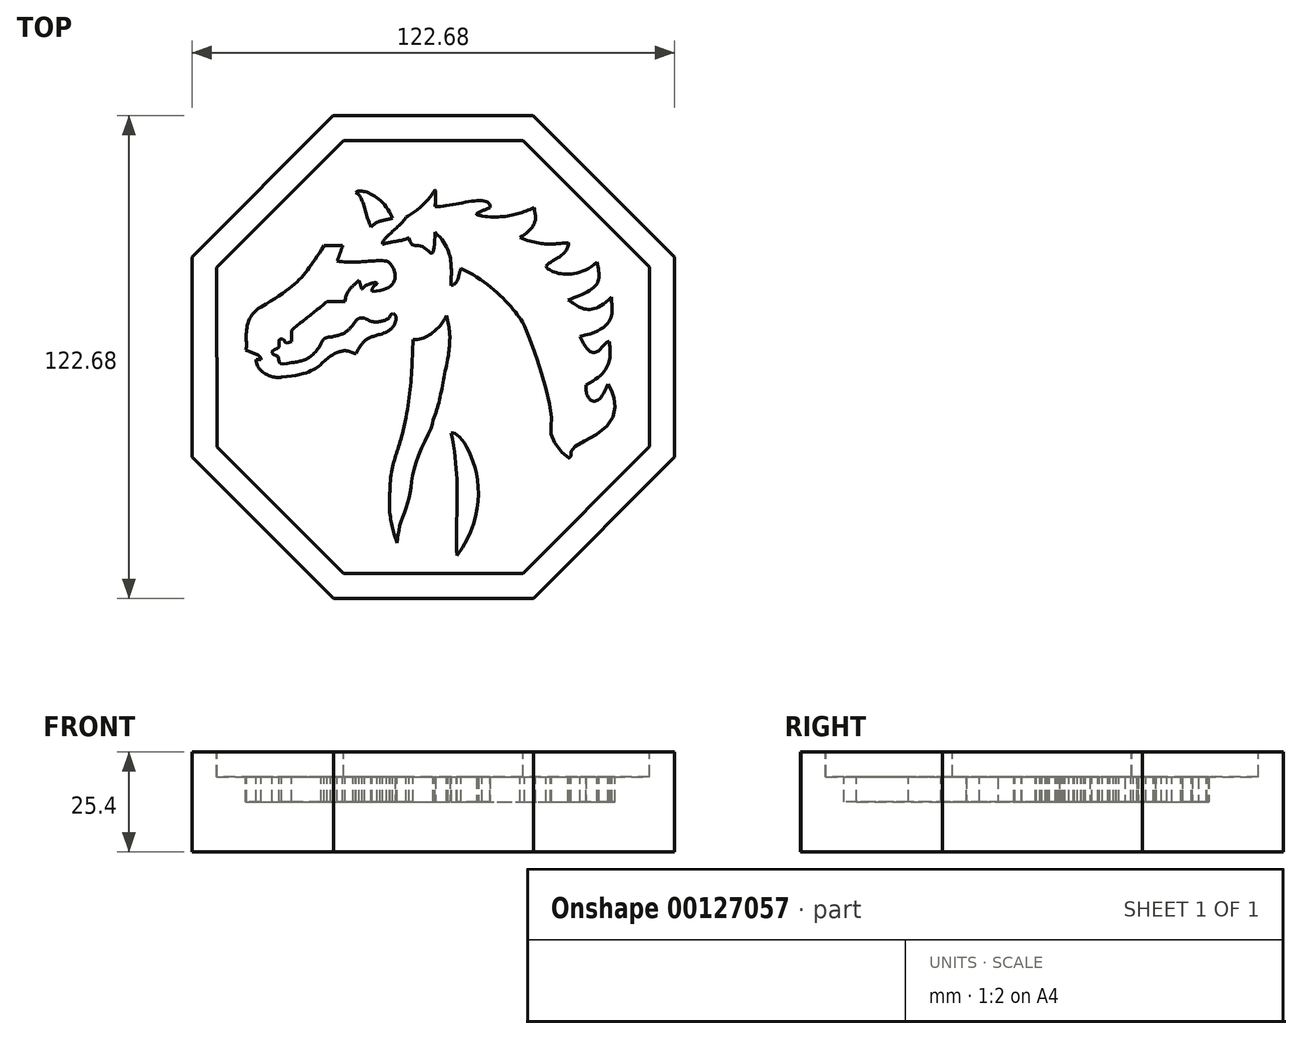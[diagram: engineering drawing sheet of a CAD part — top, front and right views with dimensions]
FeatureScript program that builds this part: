
annotation { "Feature Type Name" : "Feature", "Feature Type Description" : "" }
export const myFeature = defineFeature(function(context is Context, id is Id, definition is map)
    precondition{}
    {
        {
            var Q0;
            Q0=qCreatedBy(makeId("Top.planeOp"),FACE);
            var sketch = newSketch(context, id + "F0", { "sketchPlane" : qUnion([Q0])});
            skCircle(sketch, "E0.cCircle", {"center": v(0, 0) * mm, "radius": 61.32 * mm, "construction": true});
            skLineSegment(sketch, "E0.0", {"start": v(-61.3, -25.44) * mm, "end": v(-61.34, 25.36) * mm});
            skLineSegment(sketch, "E0.1", {"start": v(-61.34, 25.36) * mm, "end": v(-25.44, 61.3) * mm});
            skLineSegment(sketch, "E0.2", {"start": v(-25.44, 61.3) * mm, "end": v(25.36, 61.34) * mm});
            skLineSegment(sketch, "E0.3", {"start": v(25.36, 61.34) * mm, "end": v(61.3, 25.44) * mm});
            skLineSegment(sketch, "E0.4", {"start": v(61.3, 25.44) * mm, "end": v(61.34, -25.36) * mm});
            skLineSegment(sketch, "E0.5", {"start": v(61.34, -25.36) * mm, "end": v(25.44, -61.3) * mm});
            skLineSegment(sketch, "E0.6", {"start": v(25.44, -61.3) * mm, "end": v(-25.36, -61.34) * mm});
            skLineSegment(sketch, "E0.7", {"start": v(-25.36, -61.34) * mm, "end": v(-61.3, -25.44) * mm});
            skPoint(sketch, "E0.0.midPoint", {"position": v(-61.32, -0.04) * mm});
            skSolve(sketch);
        }
        {
            var Q0;
            Q0=qSketchRegion(id+"F0",true);
            extrude(context, id + "F1", {"entities" : qUnion([Q0]), "depth" : 25.4 * mm});
        }
        {
            var Q0;
            Q0=makeQuery(id+"F1.opExtrude","CAP_FACE",FACE,{"disambiguationData":[OSD([sQuery(id+"F0.wireOp",EDGE,"E0.0"),sQuery(id+"F0.wireOp",EDGE,"E0.1"),sQuery(id+"F0.wireOp",EDGE,"E0.2"),sQuery(id+"F0.wireOp",EDGE,"E0.3"),sQuery(id+"F0.wireOp",EDGE,"E0.4"),sQuery(id+"F0.wireOp",EDGE,"E0.5"),sQuery(id+"F0.wireOp",EDGE,"E0.6"),sQuery(id+"F0.wireOp",EDGE,"E0.7")])],"isStart":false});
            var sketch = newSketch(context, id + "F2", { "sketchPlane" : qUnion([Q0])});
            skLineSegment(sketch, "E1.0", {"start": v(-54.96, -22.8) * mm, "end": v(-54.99, 22.73) * mm});
            skLineSegment(sketch, "E1.1", {"start": v(-22.73, -54.99) * mm, "end": v(-54.96, -22.8) * mm});
            skLineSegment(sketch, "E1.2", {"start": v(-54.99, 22.73) * mm, "end": v(-22.8, 54.96) * mm});
            skLineSegment(sketch, "E1.3", {"start": v(22.8, -54.96) * mm, "end": v(-22.73, -54.99) * mm});
            skLineSegment(sketch, "E1.4", {"start": v(-22.8, 54.96) * mm, "end": v(22.73, 54.99) * mm});
            skLineSegment(sketch, "E1.5", {"start": v(22.73, 54.99) * mm, "end": v(54.96, 22.8) * mm});
            skLineSegment(sketch, "E1.6", {"start": v(54.96, 22.8) * mm, "end": v(54.99, -22.73) * mm});
            skLineSegment(sketch, "E1.7", {"start": v(54.99, -22.73) * mm, "end": v(22.8, -54.96) * mm});
            skSolve(sketch);
        }
        {
            var Q0;
            Q0=qSketchRegion(id+"F2",true);
            extrude(context, id + "F3", {"entities" : qUnion([Q0]), "operationType" : NewBodyOperationType.REMOVE, "oppositeDirection" : true, "depth" : 6.35 * mm});
        }
        {
            var Q0;
            Q0=makeQuery(id+"F3.boolean.opBoolean","COPY",FACE,{"derivedFrom":makeQuery(id+"F3.opExtrude","CAP_FACE",FACE,{"disambiguationData":[OSD([sQuery(id+"F2.wireOp",EDGE,"E1.0"),sQuery(id+"F2.wireOp",EDGE,"E1.1"),sQuery(id+"F2.wireOp",EDGE,"E1.2"),sQuery(id+"F2.wireOp",EDGE,"E1.3"),sQuery(id+"F2.wireOp",EDGE,"E1.4"),sQuery(id+"F2.wireOp",EDGE,"E1.5"),sQuery(id+"F2.wireOp",EDGE,"E1.6"),sQuery(id+"F2.wireOp",EDGE,"E1.7")])],"isStart":false})});
            var sketch = newSketch(context, id + "F4", { "sketchPlane" : qUnion([Q0])});
            skFitSpline(sketch, "E2", {"points": [v(-5.15, 4.45) * mm, v(3.35, 10.57) * mm], "startDerivative": vector(12.96, -0.8) * mm, "endDerivative": vector(2.4, 5.98) * mm});
            skFitSpline(sketch, "E3", {"points": [v(3.35, 10.57) * mm, v(3.8, 0) * mm], "startDerivative": vector(4.19, -14.96) * mm, "endDerivative": vector(-0.8, -9.17) * mm});
            skFitSpline(sketch, "E4", {"points": [v(-5.15, 4.45) * mm, v(-7.68, -18.75) * mm], "startDerivative": vector(-0.8, -24.13) * mm, "endDerivative": vector(-6.18, -26.52) * mm});
            skFitSpline(sketch, "E5", {"points": [v(-7.68, -18.75) * mm, v(-11.02, -33.98) * mm], "startDerivative": vector(-4.18, -17.48) * mm, "endDerivative": vector(-0.53, -21.3) * mm});
            skFitSpline(sketch, "E6", {"points": [v(-11.02, -33.98) * mm, v(-9.16, -47.18) * mm], "startDerivative": vector(-1.6, -17.3) * mm, "endDerivative": vector(4, -9.85) * mm});
            skFitSpline(sketch, "E7", {"points": [v(-9.16, -47.18) * mm, v(-8.36, -42.41) * mm, v(-6.24, -36.2) * mm, v(-4.38, -26.74) * mm, v(0, -15.97) * mm], "startDerivative": vector(2.5, 24.1) * mm, "endDerivative": vector(0, 17.06) * mm});
            skFitSpline(sketch, "E8", {"points": [v(0, -15.97) * mm, v(3.8, 0) * mm], "startDerivative": vector(5.52, 13.3) * mm, "endDerivative": vector(3.69, 15.97) * mm});
            skFitSpline(sketch, "E9", {"points": [v(-43.8, 12.7) * mm, v(-47.65, 1.8) * mm], "startDerivative": vector(-16.35, -9.37) * mm, "endDerivative": vector(-2.4, -4.39) * mm});
            skFitSpline(sketch, "E10", {"points": [v(-47.65, 1.8) * mm, v(-43.8, -0.6) * mm], "startDerivative": vector(3.86, -2.4) * mm, "endDerivative": vector(0, -4.19) * mm});
            skFitSpline(sketch, "E11", {"points": [v(-43.8, -0.6) * mm, v(-45, -0.6) * mm], "startDerivative": vector(-1.2, 0) * mm, "endDerivative": vector(-1.2, 0) * mm});
            skFitSpline(sketch, "E12", {"points": [v(-45, -0.6) * mm, v(-38.54, -5.12) * mm], "startDerivative": vector(-0.4, -10.77) * mm, "endDerivative": vector(4.79, 1.6) * mm});
            skFitSpline(sketch, "E13", {"points": [v(-38.54, -5.12) * mm, v(-24.45, 1.13) * mm], "startDerivative": vector(31.9, 2.6) * mm, "endDerivative": vector(14.22, 6.25) * mm});
            skFitSpline(sketch, "E14", {"points": [v(-24.45, 1.13) * mm, v(-19.68, 0.88) * mm], "startDerivative": vector(8.37, 3.39) * mm, "endDerivative": vector(4.65, -0.53) * mm});
            skFitSpline(sketch, "E15", {"points": [v(-19.68, 0.88) * mm, v(-13.46, 5.77) * mm], "startDerivative": vector(6.77, 12.52) * mm, "endDerivative": vector(9.37, 2.96) * mm});
            skFitSpline(sketch, "E16", {"points": [v(-13.46, 5.77) * mm, v(-9.45, 9.91) * mm], "startDerivative": vector(11.1, 2.82) * mm, "endDerivative": vector(0.19, 2.45) * mm});
            skFitSpline(sketch, "E17", {"points": [v(-9.45, 9.91) * mm, v(-10.14, 10.98) * mm, v(-11.14, 9.91) * mm], "startDerivative": vector(-0.4, 4.35) * mm, "endDerivative": vector(-0.72, -5.03) * mm});
            skFitSpline(sketch, "E18", {"points": [v(-11.14, 9.91) * mm, v(-17.42, 9.91) * mm], "startDerivative": vector(-2.63, -1.32) * mm, "endDerivative": vector(-8.1, 6.02) * mm});
            skFitSpline(sketch, "E19", {"points": [v(-17.42, 9.91) * mm, v(-20.43, 8.16) * mm], "startDerivative": vector(-2.45, 0) * mm, "endDerivative": vector(-3.95, -6.4) * mm});
            skFitSpline(sketch, "E20", {"points": [v(-20.43, 8.16) * mm, v(-26.14, 5.08) * mm], "startDerivative": vector(-3.95, -5.65) * mm, "endDerivative": vector(-8.47, -1.32) * mm});
            skFitSpline(sketch, "E21", {"points": [v(-26.14, 5.08) * mm, v(-28.52, 3.39) * mm], "startDerivative": vector(-3.01, 0.19) * mm, "endDerivative": vector(-1.13, -3.76) * mm});
            skFitSpline(sketch, "E22", {"points": [v(-28.52, 3.39) * mm, v(-36.05, -1.44) * mm], "startDerivative": vector(-6.21, -11.67) * mm, "endDerivative": vector(-8.47, -0.94) * mm});
            skFitSpline(sketch, "E23", {"points": [v(-36.05, -1.44) * mm, v(-39.06, -1.44) * mm, v(-39.44, 0) * mm, v(-40.63, 0.63) * mm, v(-40.82, 1.63) * mm, v(-39.31, 2.45) * mm, v(-39.19, 3.77) * mm, v(-38.94, 4.58) * mm, v(-38, 4.4) * mm, v(-37.56, 3.64) * mm, v(-36.05, 3.9) * mm], "startDerivative": vector(-27.29, -5.35) * mm, "endDerivative": vector(16.68, 6.36) * mm});
            skFitSpline(sketch, "E24", {"points": [v(-36.05, 3.9) * mm, v(-36.05, 6.78) * mm], "startDerivative": vector(0, 2.57) * mm, "endDerivative": vector(0, 2.57) * mm});
            skFitSpline(sketch, "E25", {"points": [v(-36.05, 6.78) * mm, v(-26.95, 14.12) * mm], "startDerivative": vector(9.22, 7.65) * mm, "endDerivative": vector(9.22, 7.65) * mm});
            skFitSpline(sketch, "E26", {"points": [v(-26.95, 14.12) * mm, v(-22.43, 14.12) * mm], "startDerivative": vector(4.7, 0) * mm, "endDerivative": vector(4.7, 0) * mm});
            skFitSpline(sketch, "E27", {"points": [v(-43.8, 12.7) * mm, v(-27.73, 28.31) * mm], "startDerivative": vector(30.6, 18.26) * mm, "endDerivative": vector(14.92, 22.74) * mm});
            skFitSpline(sketch, "E28", {"points": [v(-27.73, 28.31) * mm, v(-23, 28.31) * mm], "startDerivative": vector(4.74, 0) * mm, "endDerivative": vector(4.74, 0) * mm});
            skFitSpline(sketch, "E29", {"points": [v(-23, 28.31) * mm, v(-24.41, 24.4) * mm], "startDerivative": vector(-1.42, -3.73) * mm, "endDerivative": vector(-1.42, -3.73) * mm});
            skFitSpline(sketch, "E30", {"points": [v(-24.41, 24.4) * mm, v(-11.86, 24.4) * mm], "startDerivative": vector(15.28, -2.49) * mm, "endDerivative": vector(12.44, -1.07) * mm});
            skFitSpline(sketch, "E31", {"points": [v(-11.86, 24.4) * mm, v(-15.59, 16.65) * mm], "startDerivative": vector(5.33, -1.78) * mm, "endDerivative": vector(-27, -1.42) * mm});
            skFitSpline(sketch, "E32", {"points": [v(-22.43, 14.12) * mm, v(-18.9, 19.49) * mm], "startDerivative": vector(0.61, 8.83) * mm, "endDerivative": vector(3.2, 3.38) * mm});
            skFitSpline(sketch, "E33", {"points": [v(-18.9, 19.49) * mm, v(-18.14, 17.24) * mm], "startDerivative": vector(1.13, -2.01) * mm, "endDerivative": vector(1.13, -2.01) * mm});
            skFitSpline(sketch, "E34", {"points": [v(-18.14, 17.24) * mm, v(-14.23, 18.78) * mm], "startDerivative": vector(3.02, 3.9) * mm, "endDerivative": vector(2.3, -1.07) * mm});
            skFitSpline(sketch, "E35", {"points": [v(-14.23, 18.78) * mm, v(-15.59, 16.65) * mm], "startDerivative": vector(-1.36, -2.13) * mm, "endDerivative": vector(0, -4.09) * mm});
            skFitSpline(sketch, "E36", {"points": [v(-15.77, 33) * mm, v(-10.35, 35.3) * mm], "startDerivative": vector(4.74, 5.93) * mm, "endDerivative": vector(5.37, 2.06) * mm});
            skFitSpline(sketch, "E37", {"points": [v(-15.77, 33) * mm, v(-19.72, 41.82) * mm], "startDerivative": vector(-4.86, 8.77) * mm, "endDerivative": vector(-6.52, 2.73) * mm});
            skFitSpline(sketch, "E38", {"points": [v(-19.72, 41.82) * mm, v(-17.55, 42.06) * mm, v(-10.35, 35.3) * mm], "startDerivative": vector(3.33, 3.9) * mm, "endDerivative": vector(7.66, -18.97) * mm});
            skFitSpline(sketch, "E39", {"points": [v(-12.92, 29.06) * mm, v(-6.88, 35.58) * mm], "startDerivative": vector(2.73, 5.7) * mm, "endDerivative": vector(4.62, 7.47) * mm});
            skFitSpline(sketch, "E40", {"points": [v(-6.88, 35.58) * mm, v(0, 41.74) * mm], "startDerivative": vector(10.55, 5.7) * mm, "endDerivative": vector(5.57, 7.59) * mm});
            skFitSpline(sketch, "E41", {"points": [v(-12.92, 28.66) * mm, v(-6.17, 30.28) * mm], "startDerivative": vector(7.44, 2.3) * mm, "endDerivative": vector(6.05, 2.84) * mm});
            skFitSpline(sketch, "E42", {"points": [v(-12.92, 29.06) * mm, v(-12.92, 28.66) * mm], "startDerivative": vector(0, -0.4) * mm, "endDerivative": vector(0, -0.4) * mm});
            skFitSpline(sketch, "E43", {"points": [v(-6.17, 30.28) * mm, v(-5.17, 28.43) * mm, v(-2.75, 28.1) * mm, v(-0.42, 26.39) * mm, v(0.47, 31.69) * mm], "startDerivative": vector(3.37, -11.84) * mm, "endDerivative": vector(1.82, 25.43) * mm});
            skFitSpline(sketch, "E44", {"points": [v(0, 41.74) * mm, v(0.47, 42.38) * mm, v(0.47, 38.23) * mm], "startDerivative": vector(1.78, 3.3) * mm, "endDerivative": vector(-0.54, -8.75) * mm});
            skFitSpline(sketch, "E45", {"points": [v(0.47, 38.23) * mm, v(14.38, 38) * mm], "startDerivative": vector(14.34, -0.42) * mm, "endDerivative": vector(-0.85, -11.56) * mm});
            skFitSpline(sketch, "E46", {"points": [v(14.38, 38) * mm, v(11.75, 36.82) * mm, v(10.95, 36.21) * mm, v(12.4, 35.8) * mm], "startDerivative": vector(-6.37, -2.9) * mm, "endDerivative": vector(4.93, -2.67) * mm});
            skFitSpline(sketch, "E47", {"points": [v(12.4, 35.8) * mm, v(25.61, 37.95) * mm], "startDerivative": vector(16.78, -2.11) * mm, "endDerivative": vector(11.42, 5.08) * mm});
            skFitSpline(sketch, "E48", {"points": [v(22.04, 30.34) * mm, v(25.61, 37.95) * mm], "startDerivative": vector(14.8, 9.59) * mm, "endDerivative": vector(-1.13, 7.61) * mm});
            skFitSpline(sketch, "E49", {"points": [v(0.47, 31.69) * mm, v(4.56, 18.12) * mm], "startDerivative": vector(15.37, -14.76) * mm, "endDerivative": vector(0.42, -13.4) * mm});
            skFitSpline(sketch, "E50", {"points": [v(4.56, 18.12) * mm, v(7.05, 22.49) * mm], "startDerivative": vector(6.77, 2.26) * mm, "endDerivative": vector(2.5, 4.37) * mm});
            skFitSpline(sketch, "E51", {"points": [v(7.05, 22.49) * mm, v(23.23, 7.89) * mm], "startDerivative": vector(23.83, -10.64) * mm, "endDerivative": vector(6.13, -11.4) * mm});
            skFitSpline(sketch, "E52", {"points": [v(23.23, 7.89) * mm, v(26.68, -1.55) * mm, v(30.06, -16.34) * mm, v(30.2, -20.63) * mm, v(34.7, -25.77) * mm, v(34.92, -24.72) * mm, v(35.7, -23.03) * mm, v(44.5, -17.18) * mm, v(45.98, -10.7) * mm, v(44.36, -6.9) * mm], "startDerivative": vector(22.57, -57.18) * mm, "endDerivative": vector(-23.03, 33.4) * mm});
            skFitSpline(sketch, "E53", {"points": [v(38.83, -7.14) * mm, v(44.36, -6.9) * mm], "startDerivative": vector(-1.63, -11.18) * mm, "endDerivative": vector(8, 22.02) * mm});
            skFitSpline(sketch, "E54", {"points": [v(38.83, -7.14) * mm, v(44.7, 4) * mm], "startDerivative": vector(21.73, 11.43) * mm, "endDerivative": vector(-1, 10.3) * mm});
            skFitSpline(sketch, "E55", {"points": [v(44.7, 4) * mm, v(37.26, 5.24) * mm], "startDerivative": vector(-4.9, 0) * mm, "endDerivative": vector(-11.18, 25.25) * mm});
            skFitSpline(sketch, "E56", {"points": [v(37.26, 5.24) * mm, v(45.32, 15.3) * mm], "startDerivative": vector(32.61, 6.18) * mm, "endDerivative": vector(1.28, 6.14) * mm});
            skFitSpline(sketch, "E57", {"points": [v(34.28, 14.5) * mm, v(45.32, 15.3) * mm], "startDerivative": vector(6.38, -3.87) * mm, "endDerivative": vector(16.56, 17.76) * mm});
            skFitSpline(sketch, "E58", {"points": [v(34.28, 14.5) * mm, v(41.64, 18.74) * mm, v(41.54, 24.07) * mm], "startDerivative": vector(16.92, 6.35) * mm, "endDerivative": vector(-3.19, 13.04) * mm});
            skFitSpline(sketch, "E59", {"points": [v(28.6, 23.12) * mm, v(41.54, 24.07) * mm], "startDerivative": vector(2.24, -5.68) * mm, "endDerivative": vector(15.69, 14.5) * mm});
            skFitSpline(sketch, "E60", {"points": [v(22.04, 30.34) * mm, v(34.32, 29.05) * mm], "startDerivative": vector(15.32, -6.42) * mm, "endDerivative": vector(11.65, 1.2) * mm});
            skFitSpline(sketch, "E61", {"points": [v(28.6, 23.12) * mm, v(34.32, 29.05) * mm], "startDerivative": vector(5.73, 5.93) * mm, "endDerivative": vector(0, 10.16) * mm});
            skFitSpline(sketch, "E62", {"points": [v(4.52, -19.25) * mm, v(6.02, -50.37) * mm], "startDerivative": vector(7.9, -37.79) * mm, "endDerivative": vector(1.7, -31.68) * mm});
            skFitSpline(sketch, "E63", {"points": [v(4.52, -19.25) * mm, v(6.02, -50.37) * mm], "startDerivative": vector(9.87, 2.26) * mm, "endDerivative": vector(-34.12, -45.4) * mm});
            skSolve(sketch);
        }
        {
            var Q0;
            Q0 = qSketchRegion(id + "F4", true);
            extrude(context, id + "F5", {"entities" : qUnion([Q0]), "operationType" : NewBodyOperationType.REMOVE, "oppositeDirection" : true, "depth" : 6.35 * mm});
        }
    });
